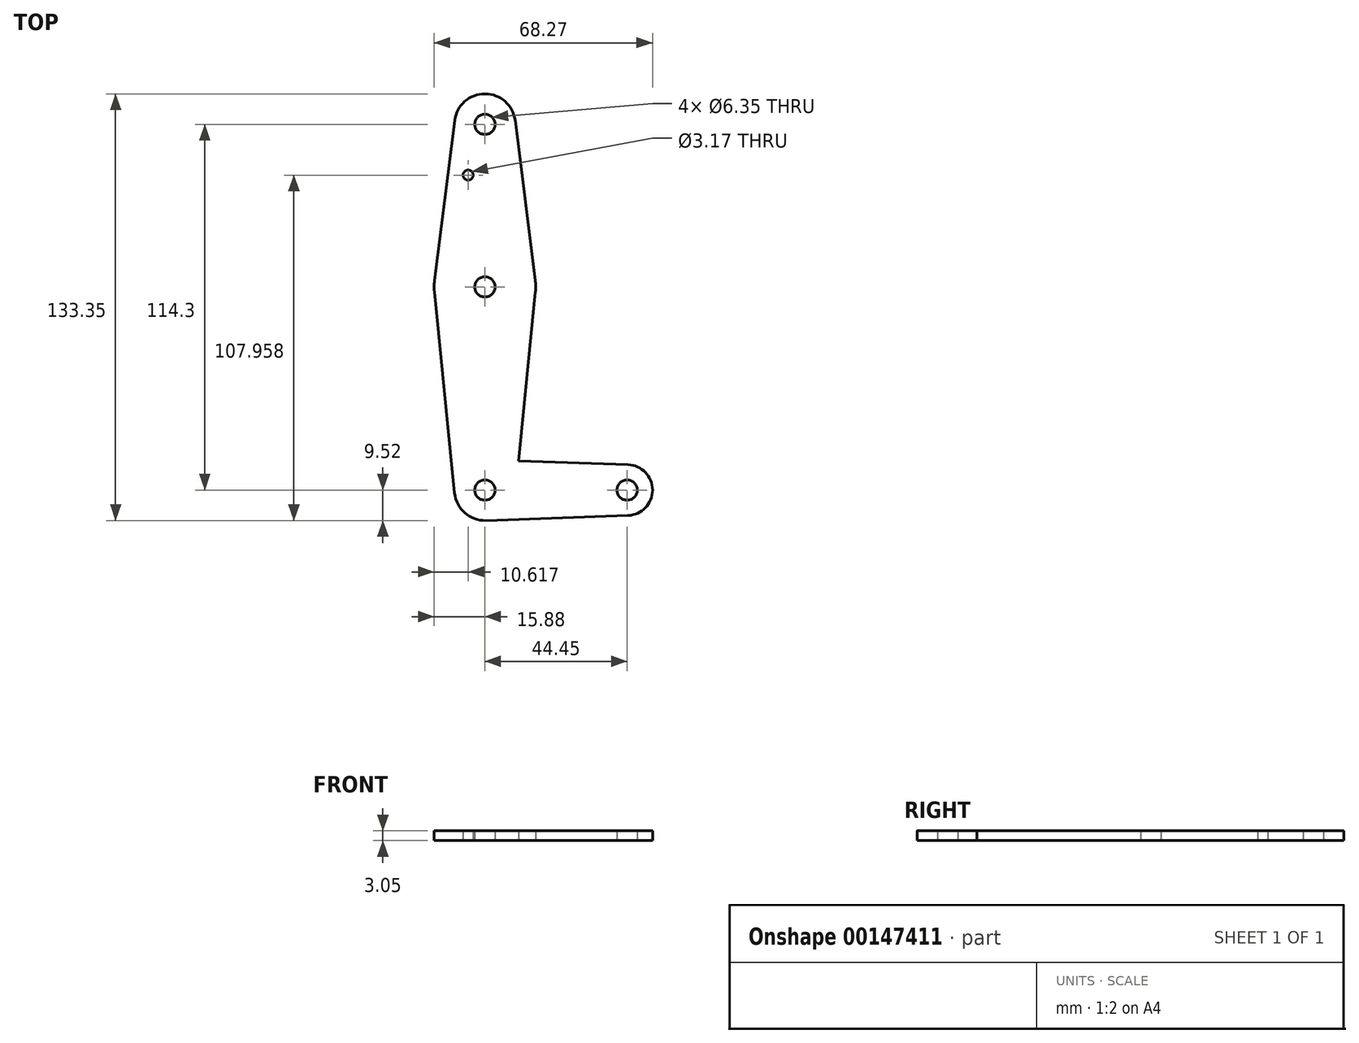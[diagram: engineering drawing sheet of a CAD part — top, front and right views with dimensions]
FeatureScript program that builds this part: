
annotation { "Feature Type Name" : "Feature", "Feature Type Description" : "" }
export const myFeature = defineFeature(function(context is Context, id is Id, definition is map)
    precondition{}
    {
        {
            var Q0;
            Q0=qCreatedBy(makeId("Top.planeOp"),FACE);
            var sketch = newSketch(context, id + "F0", { "sketchPlane" : qUnion([Q0])});
            skLineSegment(sketch, "E0", {"start": v(0, 114.3) * mm, "end": v(0, 0) * mm, "construction": true});
            skLineSegment(sketch, "E1", {"start": v(0, 0) * mm, "end": v(44.45, 0) * mm, "construction": true});
            skCircle(sketch, "E2", {"center": v(0, 114.3) * mm, "radius": 9.53 * mm});
            skCircle(sketch, "E3", {"center": v(0, 0) * mm, "radius": 9.53 * mm});
            skCircle(sketch, "E4", {"center": v(44.45, 0) * mm, "radius": 7.94 * mm});
            skCircle(sketch, "E5", {"center": v(0, 63.5) * mm, "radius": 15.88 * mm});
            skLineSegment(sketch, "E6", {"start": v(-9.45, 115.5) * mm, "end": v(-15.75, 65.48) * mm});
            skLineSegment(sketch, "E7", {"start": v(9.45, 115.5) * mm, "end": v(15.75, 65.48) * mm});
            skLineSegment(sketch, "E8", {"start": v(-15.8, 61.91) * mm, "end": v(-9.48, -0.95) * mm});
            skLineSegment(sketch, "E9", {"start": v(9.48, -0.95) * mm, "end": v(15.8, 61.91) * mm});
            skLineSegment(sketch, "E10", {"start": v(44.73, 7.93) * mm, "end": v(0.34, 9.52) * mm});
            skLineSegment(sketch, "E11", {"start": v(0.34, -9.52) * mm, "end": v(44.73, -7.93) * mm});
            skCircle(sketch, "E12", {"center": v(0, 114.3) * mm, "radius": 3.18 * mm});
            skCircle(sketch, "E13", {"center": v(0, 63.5) * mm, "radius": 3.18 * mm});
            skCircle(sketch, "E14", {"center": v(0, 0) * mm, "radius": 3.18 * mm});
            skCircle(sketch, "E15", {"center": v(44.45, 0) * mm, "radius": 3.18 * mm});
            skCircle(sketch, "E16", {"center": v(-5.26, 98.44) * mm, "radius": 1.59 * mm});
            skLineSegment(sketch, "E17", {"start": v(-5.26, 98.44) * mm, "end": v(-5.26, 61.91) * mm});
            skSolve(sketch);
        }
        {
            var Q0;
            Q0 = qSketchRegion(id + "F0", true);
            extrude(context, id + "F1", {"entities" : qUnion([Q0]), "depth" : 3.05 * mm});
        }
    });
